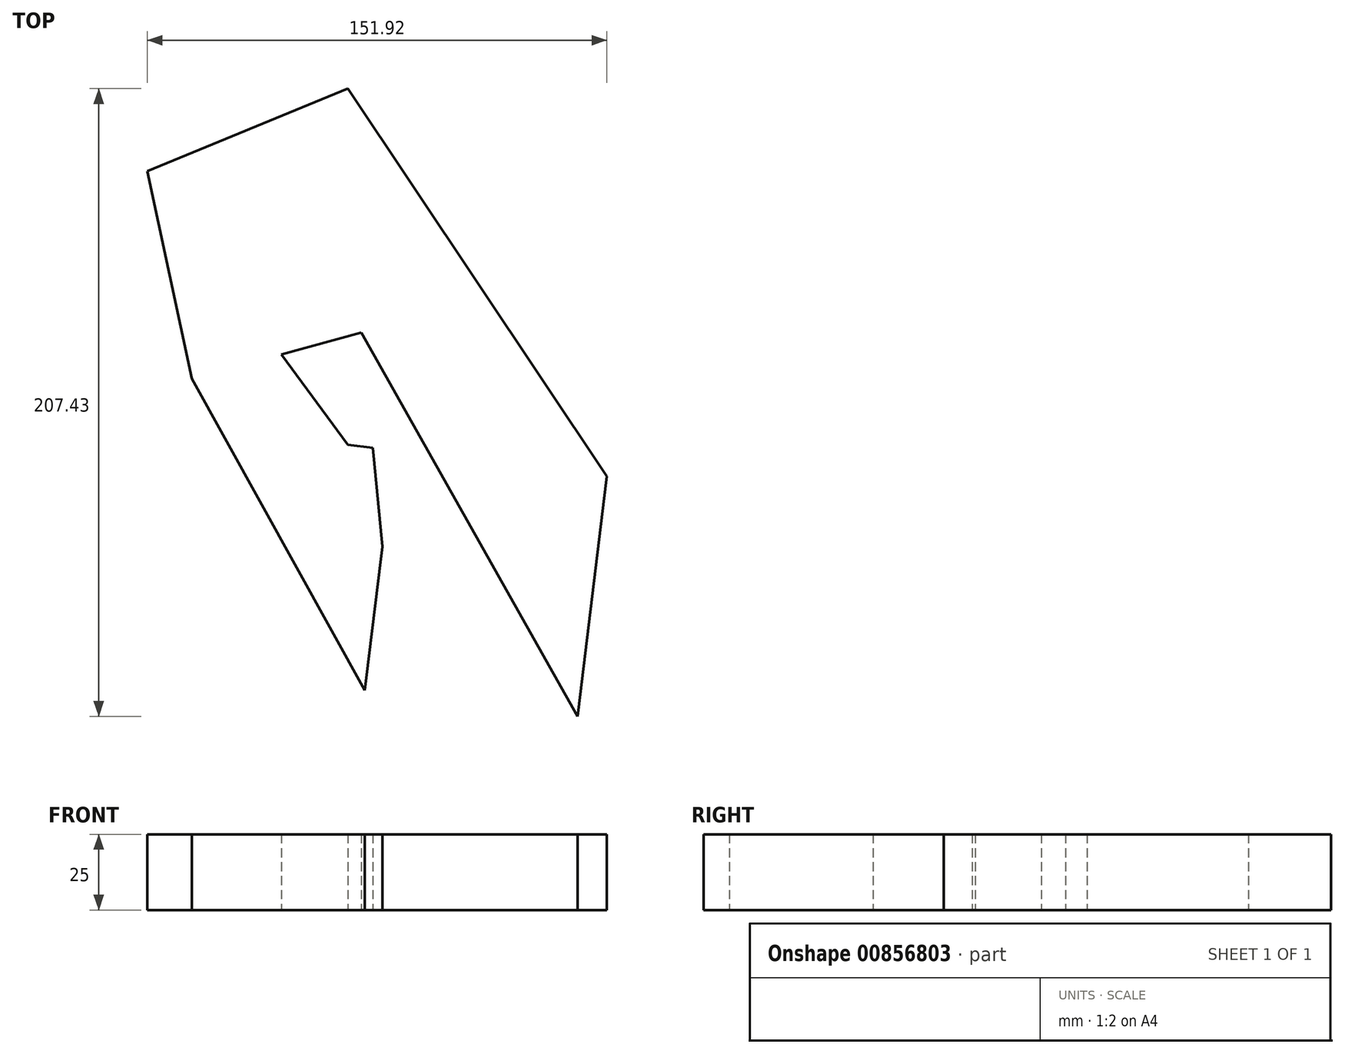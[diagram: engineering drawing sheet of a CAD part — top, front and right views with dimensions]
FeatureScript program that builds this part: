
annotation { "Feature Type Name" : "Feature", "Feature Type Description" : "" }
export const myFeature = defineFeature(function(context is Context, id is Id, definition is map)
    precondition{}
    {
        {
            var Q0;
            Q0=qCreatedBy(makeId("Top.planeOp"),FACE);
            var sketch = newSketch(context, id + "F0", { "sketchPlane" : qUnion([Q0])});
            skLineSegment(sketch, "E0", {"start": v(-56.53, 50.96) * mm, "end": v(29.02, 40.57) * mm});
            skLineSegment(sketch, "E1", {"start": v(29.02, 40.57) * mm, "end": v(19.38, -38.8) * mm});
            skLineSegment(sketch, "E2", {"start": v(19.38, -38.8) * mm, "end": v(-50.94, -30.25) * mm});
            skLineSegment(sketch, "E3", {"start": v(-50.94, -30.25) * mm, "end": v(-56.53, 50.96) * mm});
            skLineSegment(sketch, "E4", {"start": v(-56.53, 50.96) * mm, "end": v(-122.9, 141.34) * mm});
            skLineSegment(sketch, "E5", {"start": v(-122.9, 141.34) * mm, "end": v(-56.53, 168.63) * mm});
            skLineSegment(sketch, "E6", {"start": v(-56.53, 168.63) * mm, "end": v(29.02, 40.57) * mm});
            skLineSegment(sketch, "E7", {"start": v(19.38, -38.8) * mm, "end": v(-52.07, 88) * mm});
            skLineSegment(sketch, "E8", {"start": v(-52.07, 88) * mm, "end": v(-23.81, 106.87) * mm});
            skLineSegment(sketch, "E9", {"start": v(-23.81, 106.87) * mm, "end": v(29.02, 40.57) * mm});
            skLineSegment(sketch, "E10", {"start": v(-50.94, -30.25) * mm, "end": v(-45.17, 17.24) * mm});
            skLineSegment(sketch, "E11", {"start": v(-45.17, 17.24) * mm, "end": v(-52.07, 88) * mm});
            skLineSegment(sketch, "E12", {"start": v(-23.81, 106.87) * mm, "end": v(-56.53, 168.63) * mm});
            skLineSegment(sketch, "E13", {"start": v(-122.9, 141.34) * mm, "end": v(-52.07, 88) * mm});
            skLineSegment(sketch, "E14", {"start": v(-50.94, -30.25) * mm, "end": v(-108.17, 72.83) * mm});
            skLineSegment(sketch, "E15", {"start": v(-108.17, 72.83) * mm, "end": v(-56.53, 50.96) * mm});
            skLineSegment(sketch, "E16", {"start": v(-108.17, 72.83) * mm, "end": v(-122.9, 141.34) * mm});
            skLineSegment(sketch, "E17", {"start": v(-108.17, 72.83) * mm, "end": v(-52.07, 88) * mm});
            skSolve(sketch);
        }
        {
            var Q0;
            {var subQ0=sQuery(id+"F0.wireOp",EDGE,"E1");Q0=makeQuery(id+"F0.imprint","IMPRINT",FACE,{"disambiguationData":[TD([[makeQuery(id+"F0.imprint","IMPRINT",EDGE,{"derivedFrom":subQ0}),-1.0]])]});}
            var Q1;
            Q1=makeQuery(id+"F0.imprint","IMPRINT",FACE,{"disambiguationData":[TD([[makeQuery(id+"F0.imprint","IMPRINT",EDGE,{"derivedFrom":sQuery(id+"F0.wireOp",EDGE,"E3")}),1.0]])]});
            var Q2;
            {var subQ0=sQuery(id+"F0.wireOp",EDGE,"E16");Q2=makeQuery(id+"F0.imprint","IMPRINT",FACE,{"disambiguationData":[TD([[makeQuery(id+"F0.imprint","IMPRINT",EDGE,{"derivedFrom":subQ0}),-1.0]])]});}
            var Q3;
            Q3=makeQuery(id+"F0.imprint","IMPRINT",FACE,{"disambiguationData":[TD([[makeQuery(id+"F0.imprint","IMPRINT",EDGE,{"derivedFrom":sQuery(id+"F0.wireOp",EDGE,"E6")}),-1.0]])]});
            var Q4;
            {var subQ0=sQuery(id+"F0.wireOp",EDGE,"E3");Q4=makeQuery(id+"F0.imprint","IMPRINT",FACE,{"disambiguationData":[TD([[makeQuery(id+"F0.imprint","IMPRINT",EDGE,{"derivedFrom":subQ0}),-1.0]])]});}
            var Q5;
            {var subQ0=sQuery(id+"F0.wireOp",EDGE,"E15");Q5=makeQuery(id+"F0.imprint","IMPRINT",FACE,{"disambiguationData":[TD([[makeQuery(id+"F0.imprint","IMPRINT",EDGE,{"derivedFrom":subQ0}),1.0]])]});}
            var Q6;
            {var subQ0=sQuery(id+"F0.wireOp",EDGE,"E13");Q6=makeQuery(id+"F0.imprint","IMPRINT",FACE,{"disambiguationData":[TD([[makeQuery(id+"F0.imprint","IMPRINT",EDGE,{"derivedFrom":subQ0}),-1.0]])]});}
            var Q7;
            Q7=makeQuery(id+"F0.imprint","IMPRINT",FACE,{"disambiguationData":[TD([[makeQuery(id+"F0.imprint","IMPRINT",EDGE,{"derivedFrom":sQuery(id+"F0.wireOp",EDGE,"E5")}),-1.0]])]});
            var Q8;
            {var subQ4=sQuery(id+"F0.wireOp",EDGE,"E8");Q8=makeQuery(id+"F0.imprint","IMPRINT",FACE,{"disambiguationData":[TD([[makeQuery(id+"F0.imprint","IMPRINT",EDGE,{"derivedFrom":subQ4}),-1.0]])]});}
            extrude(context, id + "F1", {"entities" : qUnion([Q0, Q1, Q2, Q3, Q4, Q5, Q6, Q7, Q8]), "depth" : 25 * mm, "offsetDistance" : 25 * mm});
        }
    });
